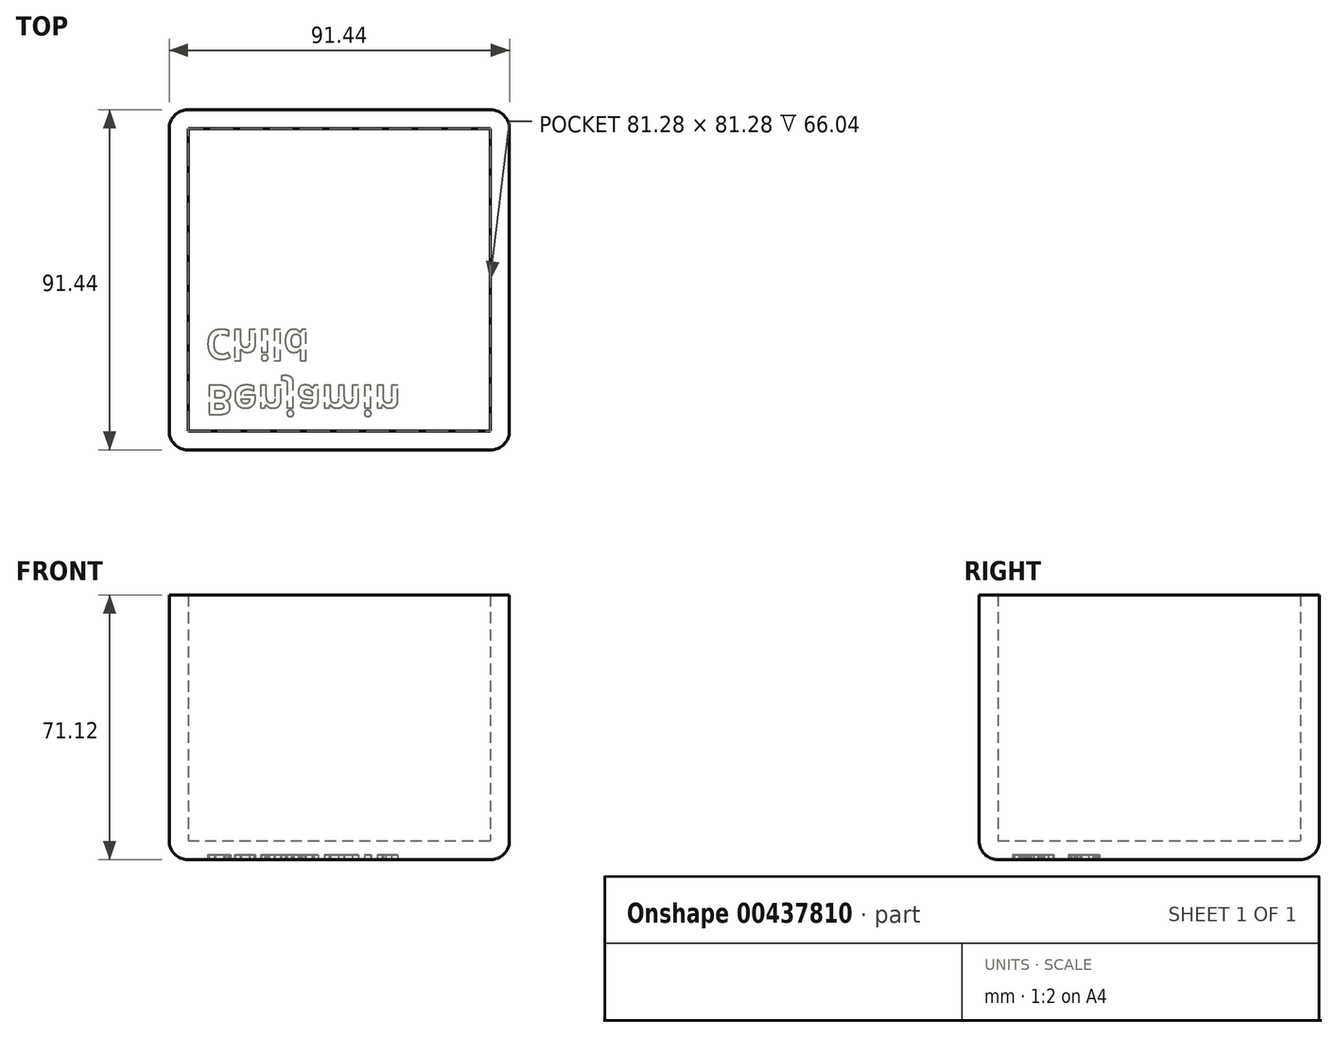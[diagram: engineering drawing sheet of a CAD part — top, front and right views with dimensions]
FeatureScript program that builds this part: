
annotation { "Feature Type Name" : "Feature", "Feature Type Description" : "" }
export const myFeature = defineFeature(function(context is Context, id is Id, definition is map)
    precondition{}
    {
        {
            var Q0;
            Q0=qCreatedBy(makeId("Top.planeOp"),FACE);
            var sketch = newSketch(context, id + "F0", { "sketchPlane" : qUnion([Q0])});
            skLineSegment(sketch, "E0.bottom", {"start": v(-24.18, -25.55) * mm, "end": v(57.1, -25.55) * mm});
            skLineSegment(sketch, "E0.top", {"start": v(-24.18, 55.73) * mm, "end": v(57.1, 55.73) * mm});
            skLineSegment(sketch, "E0.left", {"start": v(-24.18, -25.55) * mm, "end": v(-24.18, 55.73) * mm});
            skLineSegment(sketch, "E0.right", {"start": v(57.1, -25.55) * mm, "end": v(57.1, 55.73) * mm});
            skLineSegment(sketch, "E1.bottom", {"start": v(-29.26, 60.8) * mm, "end": v(62.18, 60.8) * mm});
            skLineSegment(sketch, "E1.top", {"start": v(-29.26, -30.63) * mm, "end": v(62.18, -30.63) * mm});
            skLineSegment(sketch, "E1.left", {"start": v(-29.26, 60.8) * mm, "end": v(-29.26, -30.63) * mm});
            skLineSegment(sketch, "E1.right", {"start": v(62.18, 60.8) * mm, "end": v(62.18, -30.63) * mm});
            skSolve(sketch);
        }
        {
            var Q0;
            Q0=makeQuery(id+"F0.imprint","IMPRINT",FACE,{"disambiguationData":[TD([[makeQuery(id+"F0.imprint","IMPRINT",EDGE,{"derivedFrom":sQuery(id+"F0.wireOp",EDGE,"E0.bottom")}),-1.0]])]});
            extrude(context, id + "F1", {"entities" : qUnion([Q0]), "depth" : 71.12 * mm});
        }
        {
            var Q0;
            Q0=makeQuery(id+"F0.imprint","IMPRINT",FACE,{"disambiguationData":[TD([[makeQuery(id+"F0.imprint","IMPRINT",EDGE,{"derivedFrom":sQuery(id+"F0.wireOp",EDGE,"E0.bottom")}),1.0]])]});
            extrude(context, id + "F2", {"entities" : qUnion([Q0]), "operationType" : NewBodyOperationType.ADD, "depth" : 5.08 * mm});
        }
        {
            var Q0;
            Q0=makeQuery(id+"F1.opExtrude","SWEPT_EDGE",EDGE,{"disambiguationData":[OSD([sQuery(id+"F0.wireOp",EDGE,"E1.bottom"),sQuery(id+"F0.wireOp",EDGE,"E1.right")])]});
            var Q1;
            Q1=makeQuery(id+"F1.opExtrude","SWEPT_EDGE",EDGE,{"disambiguationData":[OSD([sQuery(id+"F0.wireOp",EDGE,"E1.bottom"),sQuery(id+"F0.wireOp",EDGE,"E1.left")])]});
            var Q2;
            Q2=makeQuery(id+"F1.opExtrude","SWEPT_EDGE",EDGE,{"disambiguationData":[OSD([sQuery(id+"F0.wireOp",EDGE,"E1.top"),sQuery(id+"F0.wireOp",EDGE,"E1.left")])]});
            var Q3;
            Q3=makeQuery(id+"F1.opExtrude","SWEPT_EDGE",EDGE,{"disambiguationData":[OSD([sQuery(id+"F0.wireOp",EDGE,"E1.top"),sQuery(id+"F0.wireOp",EDGE,"E1.right")])]});
            var Q4;
            Q4=makeQuery(id+"F1.opExtrude","CAP_EDGE",EDGE,{"disambiguationData":[OSD([sQuery(id+"F0.wireOp",EDGE,"E1.right")])],"isStart":true});
            var Q5;
            Q5=makeQuery(id+"F1.opExtrude","CAP_EDGE",EDGE,{"disambiguationData":[OSD([sQuery(id+"F0.wireOp",EDGE,"E1.top")])],"isStart":true});
            var Q6;
            Q6=makeQuery(id+"F1.opExtrude","CAP_EDGE",EDGE,{"disambiguationData":[OSD([sQuery(id+"F0.wireOp",EDGE,"E1.left")])],"isStart":true});
            var Q7;
            Q7=makeQuery(id+"F1.opExtrude","CAP_EDGE",EDGE,{"disambiguationData":[OSD([sQuery(id+"F0.wireOp",EDGE,"E1.bottom")])],"isStart":true});
            fillet(context, id + "F3", {"entities" : qUnion([Q0, Q1, Q2, Q3, Q4, Q5, Q6, Q7]), "radius" : 5.08 * mm, "tangentPropagation" : true, "allowEdgeOverflow" : false});
        }
        {
            var Q0;
            {var subQ0=sQuery(id+"F0.wireOp",EDGE,"E0.right");var subQ1=sQuery(id+"F0.wireOp",EDGE,"E0.left");var subQ2=sQuery(id+"F0.wireOp",EDGE,"E0.top");var subQ3=sQuery(id+"F0.wireOp",EDGE,"E0.bottom");Q0=makeQuery(id+"F2.boolean.opBoolean","MERGE",FACE,{"derivedFrom":[makeQuery(id+"F1.opExtrude","CAP_FACE",FACE,{"disambiguationData":[OSD([subQ3,subQ2,subQ1,subQ0,sQuery(id+"F0.wireOp",EDGE,"E1.bottom"),sQuery(id+"F0.wireOp",EDGE,"E1.top"),sQuery(id+"F0.wireOp",EDGE,"E1.left"),sQuery(id+"F0.wireOp",EDGE,"E1.right")])],"isStart":true}),makeQuery(id+"F2.opExtrude","CAP_FACE",FACE,{"disambiguationData":[OSD([subQ3,subQ2,subQ1,subQ0])],"isStart":true})]});}
            var sketch = newSketch(context, id + "F4", { "sketchPlane" : qUnion([Q0])});
            skText(sketch, "E2", { "text": "Benjamin\nChild", "fontName": "OpenSans-Bold.ttf"});
            const initialGuessF4  = {"E2": [-0.0195, 0.01326, 1, 0, 0.00792]};
            skSetInitialGuess(sketch, initialGuessF4);
            skSolve(sketch);
        }
        {
            var Q0;
            Q0 = qSketchRegion(id + "F4", true);
            extrude(context, id + "F5", {"entities" : qUnion([Q0]), "operationType" : NewBodyOperationType.REMOVE, "oppositeDirection" : true, "depth" : 1.27 * mm});
        }
    });
